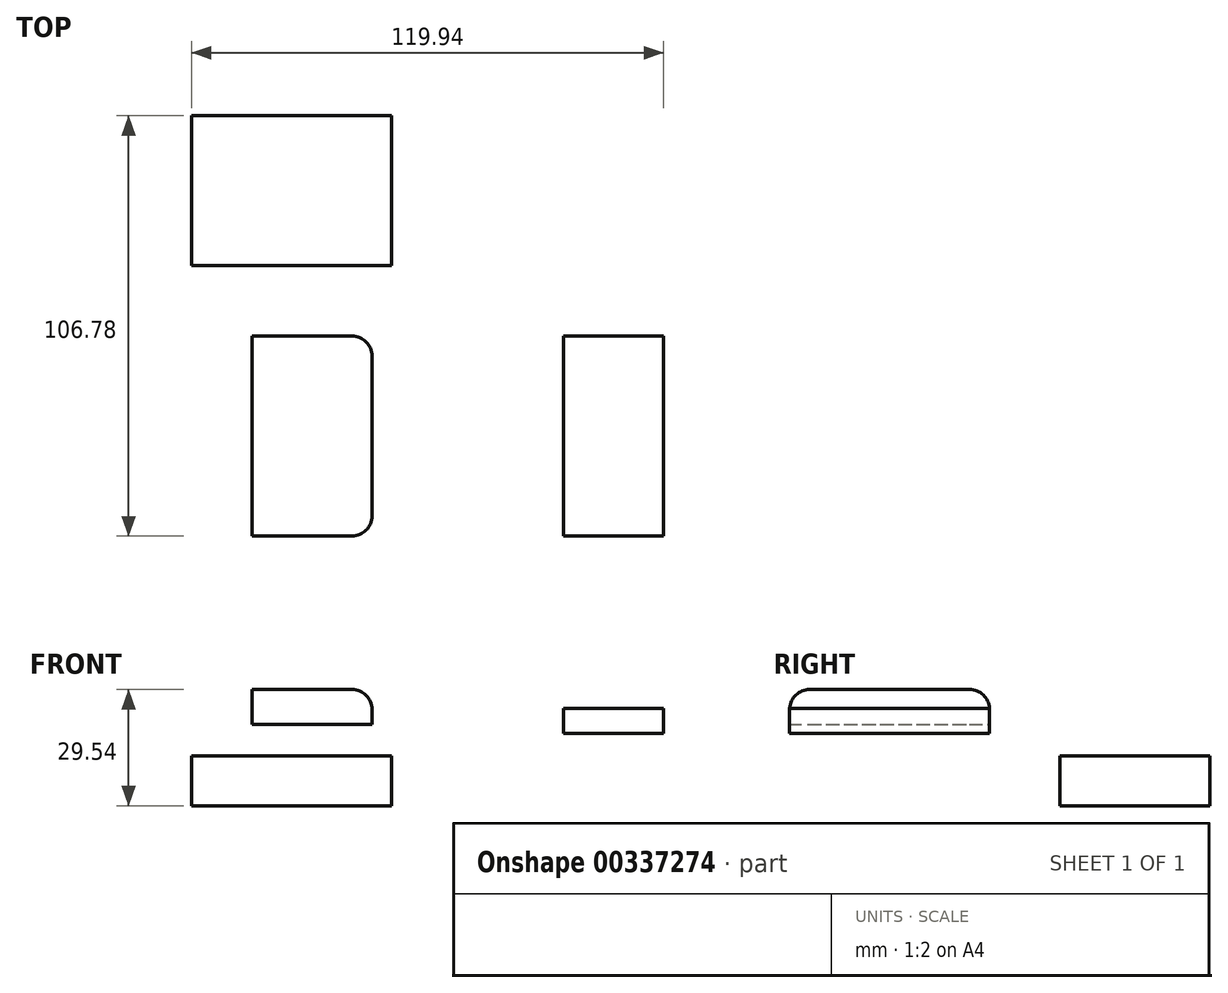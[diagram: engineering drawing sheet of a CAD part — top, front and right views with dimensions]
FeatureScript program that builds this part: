
annotation { "Feature Type Name" : "Feature", "Feature Type Description" : "" }
export const myFeature = defineFeature(function(context is Context, id is Id, definition is map)
    precondition{}
    {
        {
            var Q0;
            Q0=qCreatedBy(makeId("Front.planeOp"),FACE);
            var sketch = newSketch(context, id + "F0", { "sketchPlane" : qUnion([Q0])});
            skLineSegment(sketch, "E0.bottom", {"start": v(-46.7, 29.54) * mm, "end": v(-16.22, 29.54) * mm});
            skLineSegment(sketch, "E0.top", {"start": v(-46.7, 20.65) * mm, "end": v(-16.22, 20.65) * mm});
            skLineSegment(sketch, "E0.left", {"start": v(-46.7, 29.54) * mm, "end": v(-46.7, 20.65) * mm});
            skLineSegment(sketch, "E0.right", {"start": v(-16.22, 29.54) * mm, "end": v(-16.22, 20.65) * mm});
            skSolve(sketch);
        }
        {
            var Q0;
            Q0 = qSketchRegion(id + "F0", true);
            extrude(context, id + "F1", {"entities" : qUnion([Q0]), "depth" : 50.8 * mm});
        }
        {
            var Q0;
            Q0=makeQuery(id+"F1.opExtrude","SWEPT_EDGE",EDGE,{"disambiguationData":[OSD([sQuery(id+"F0.wireOp",EDGE,"E0.bottom"),sQuery(id+"F0.wireOp",EDGE,"E0.right")])]});
            var Q1;
            Q1=makeQuery(id+"F1.opExtrude","CAP_EDGE",EDGE,{"disambiguationData":[OSD([sQuery(id+"F0.wireOp",EDGE,"E0.bottom")])],"isStart":false});
            var Q2;
            Q2=makeQuery(id+"F1.opExtrude","CAP_EDGE",EDGE,{"disambiguationData":[OSD([sQuery(id+"F0.wireOp",EDGE,"E0.right")])],"isStart":false});
            var Q3;
            Q3=makeQuery(id+"F1.opExtrude","CAP_EDGE",EDGE,{"disambiguationData":[OSD([sQuery(id+"F0.wireOp",EDGE,"E0.bottom")])],"isStart":true});
            var Q4;
            Q4=makeQuery(id+"F1.opExtrude","CAP_EDGE",EDGE,{"disambiguationData":[OSD([sQuery(id+"F0.wireOp",EDGE,"E0.right")])],"isStart":true});
            fillet(context, id + "F2", {"entities" : qUnion([Q0, Q1, Q2, Q3, Q4]), "radius" : 5.08 * mm, "tangentPropagation" : true, "allowEdgeOverflow" : false});
        }
        {
            var Q0;
            Q0=qCreatedBy(makeId("Front.planeOp"),FACE);
            var sketch = newSketch(context, id + "F3", { "sketchPlane" : qUnion([Q0])});
            skLineSegment(sketch, "E1.bottom", {"start": v(32.49, 24.79) * mm, "end": v(57.89, 24.79) * mm});
            skLineSegment(sketch, "E1.top", {"start": v(32.49, 18.44) * mm, "end": v(57.89, 18.44) * mm});
            skLineSegment(sketch, "E1.left", {"start": v(32.49, 24.79) * mm, "end": v(32.49, 18.44) * mm});
            skLineSegment(sketch, "E1.right", {"start": v(57.89, 24.79) * mm, "end": v(57.89, 18.44) * mm});
            skSolve(sketch);
        }
        {
            var Q0;
            Q0 = qSketchRegion(id + "F3", true);
            extrude(context, id + "F4", {"entities" : qUnion([Q0]), "depth" : 50.8 * mm});
        }
        {
            var Q0;
            Q0=qCreatedBy(makeId("Top.planeOp"),FACE);
            var sketch = newSketch(context, id + "F5", { "sketchPlane" : qUnion([Q0])});
            skLineSegment(sketch, "E2.bottom", {"start": v(-62.05, 55.98) * mm, "end": v(-11.25, 55.98) * mm});
            skLineSegment(sketch, "E2.top", {"start": v(-62.05, 17.88) * mm, "end": v(-11.25, 17.88) * mm});
            skLineSegment(sketch, "E2.left", {"start": v(-62.05, 55.98) * mm, "end": v(-62.05, 17.88) * mm});
            skLineSegment(sketch, "E2.right", {"start": v(-11.25, 55.98) * mm, "end": v(-11.25, 17.88) * mm});
            skSolve(sketch);
        }
        {
            var Q0;
            Q0 = qSketchRegion(id + "F5", true);
            extrude(context, id + "F6", {"entities" : qUnion([Q0]), "depth" : 12.7 * mm});
        }
    });
